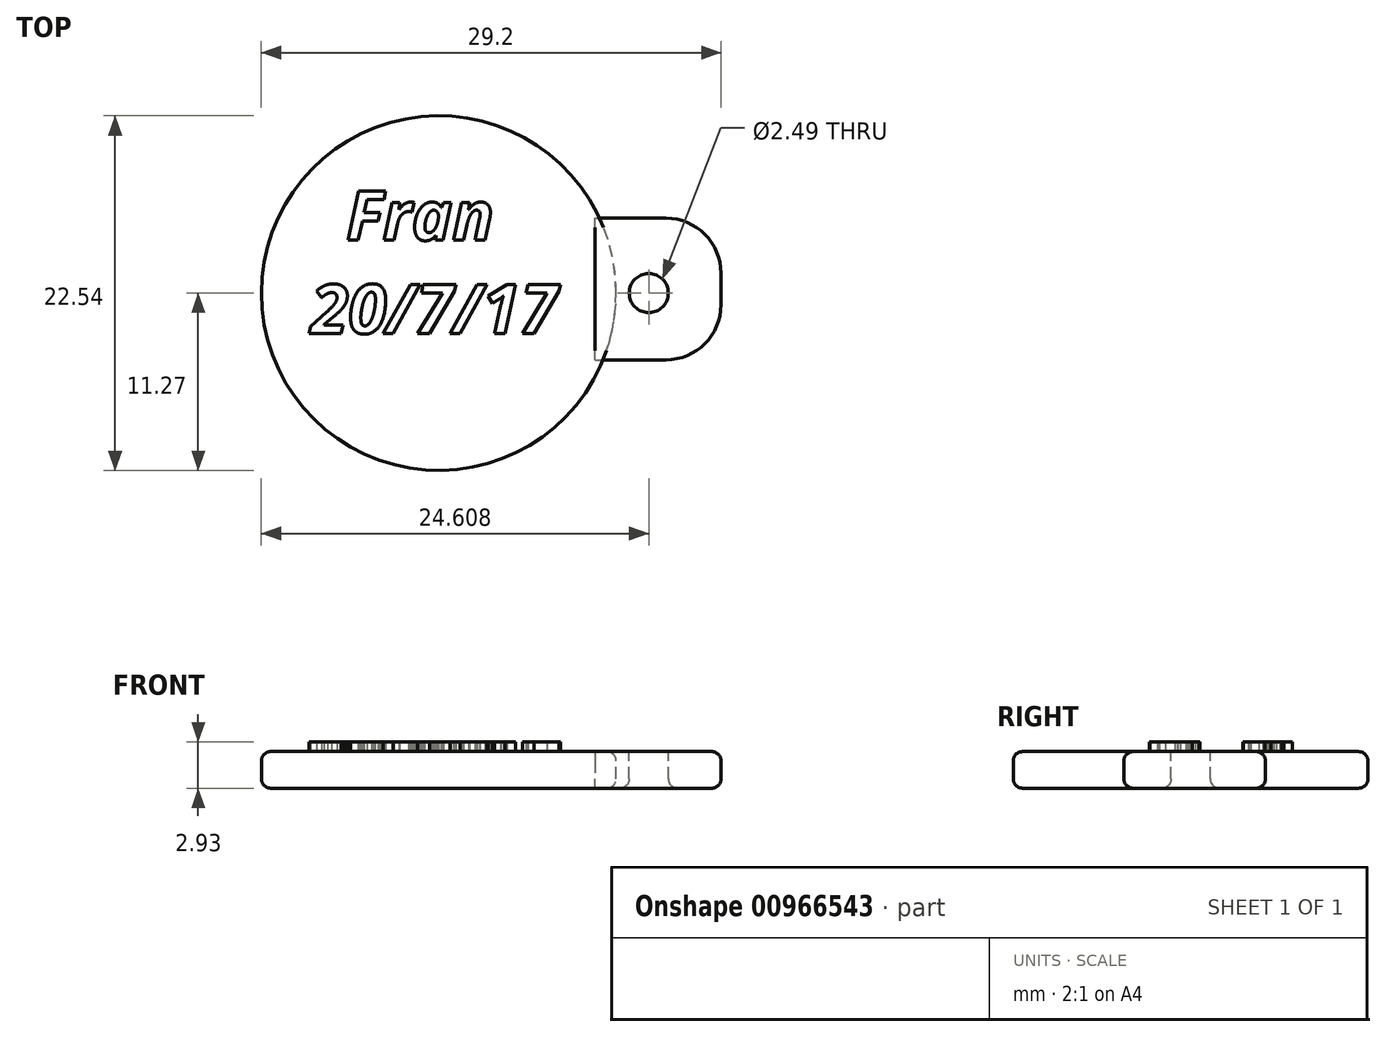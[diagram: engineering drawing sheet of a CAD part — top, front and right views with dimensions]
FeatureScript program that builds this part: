
annotation { "Feature Type Name" : "Feature", "Feature Type Description" : "" }
export const myFeature = defineFeature(function(context is Context, id is Id, definition is map)
    precondition{}
    {
        {
            var Q0;
            Q0=qCreatedBy(makeId("Front.planeOp"),FACE);
            var sketch = newSketch(context, id + "F0", { "sketchPlane" : qUnion([Q0])});
            skLineSegment(sketch, "E0", {"start": v(0, 0) * mm, "end": v(11.27, 0) * mm});
            skLineSegment(sketch, "E1", {"start": v(11.27, 0) * mm, "end": v(11.27, 2.33) * mm});
            skLineSegment(sketch, "E2", {"start": v(11.27, 2.33) * mm, "end": v(0, 2.33) * mm});
            skLineSegment(sketch, "E3", {"start": v(0, 2.33) * mm, "end": v(0, 0) * mm});
            skSolve(sketch);
        }
        {
            var Q0;
            Q0=makeQuery(id+"F0.imprint","IMPRINT",FACE,{"disambiguationData":[TD([[makeQuery(id+"F0.imprint","IMPRINT",EDGE,{"derivedFrom":sQuery(id+"F0.wireOp",EDGE,"E0")}),1.0]])]});
            var Q1;
            Q1=sQuery(id+"F0.wireOp",EDGE,"E3");
            revolve(context, id + "F1", {"surfaceOperationType" : NewSurfaceOperationType.NEW, "entities" : qUnion([Q0]), "axis" : qUnion([Q1]), "revolveType" : RevolveType.FULL});
        }
        {
            var Q0;
            Q0=makeQuery(id+"F1.opRevolve","SWEPT_FACE",FACE,{"disambiguationData":[OSD([sQuery(id+"F0.wireOp",EDGE,"E2")])]});
            var sketch = newSketch(context, id + "F2", { "sketchPlane" : qUnion([Q0])});
            skText(sketch, "E4", { "text": "  Fran\n20/7/17", "fontName": "OpenSans-BoldItalic.ttf"});
            const initialGuessF2  = {"E4": [-0.00814, 0.00336, 1, 0, 0.00314]};
            skSetInitialGuess(sketch, initialGuessF2);
            skSolve(sketch);
        }
        {
            var Q0;
            Q0 = qSketchRegion(id + "F2", true);
            extrude(context, id + "F3", {"entities" : qUnion([Q0]), "operationType" : NewBodyOperationType.ADD, "depth" : 0.6 * mm, "offsetDistance" : 25 * mm});
        }
        {
            var Q0;
            Q0=qCreatedBy(makeId("Top.planeOp"),FACE);
            var sketch = newSketch(context, id + "F4", { "sketchPlane" : qUnion([Q0])});
            skLineSegment(sketch, "E5.bottom", {"start": v(9.93, 4.76) * mm, "end": v(17.93, 4.76) * mm});
            skLineSegment(sketch, "E5.top", {"start": v(9.93, -4.24) * mm, "end": v(17.93, -4.24) * mm});
            skLineSegment(sketch, "E5.left", {"start": v(9.93, 4.76) * mm, "end": v(9.93, -4.24) * mm});
            skLineSegment(sketch, "E5.right", {"start": v(17.93, 4.76) * mm, "end": v(17.93, -4.24) * mm});
            skSolve(sketch);
        }
        {
            var Q0;
            Q0=makeQuery(id+"F4.imprint","IMPRINT",FACE,{"disambiguationData":[TD([[makeQuery(id+"F4.imprint","IMPRINT",EDGE,{"derivedFrom":sQuery(id+"F4.wireOp",EDGE,"E5.bottom")}),-1.0]])]});
            extrude(context, id + "F5", {"entities" : qUnion([Q0]), "depth" : 2.33 * mm, "offsetDistance" : 25 * mm});
        }
        {
            var Q0;
            Q0=makeQuery(id+"F5.opExtrude","CAP_FACE",FACE,{"disambiguationData":[OSD([sQuery(id+"F4.wireOp",EDGE,"E5.bottom"),sQuery(id+"F4.wireOp",EDGE,"E5.top"),sQuery(id+"F4.wireOp",EDGE,"E5.left"),sQuery(id+"F4.wireOp",EDGE,"E5.right")])],"isStart":false});
            var sketch = newSketch(context, id + "F6", { "sketchPlane" : qUnion([Q0])});
            skCircle(sketch, "E6", {"center": v(13.34, 0) * mm, "radius": 1.24 * mm});
            skSolve(sketch);
        }
        {
            var Q0;
            Q0=makeQuery(id+"F6.imprint","IMPRINT",FACE,{"disambiguationData":[TD([[makeQuery(id+"F6.imprint","IMPRINT",EDGE,{"derivedFrom":sQuery(id+"F6.wireOp",EDGE,"E6")}),1.0]])]});
            extrude(context, id + "F7", {"entities" : qUnion([Q0]), "operationType" : NewBodyOperationType.REMOVE, "endBound" : BoundingType.THROUGH_ALL, "oppositeDirection" : true, "depth" : 25 * mm, "offsetDistance" : 25 * mm});
        }
        {
            var Q0;
            Q0=makeQuery(id+"F5.opExtrude","SWEPT_EDGE",EDGE,{"disambiguationData":[OSD([sQuery(id+"F4.wireOp",EDGE,"E5.top"),sQuery(id+"F4.wireOp",EDGE,"E5.right")])]});
            var Q1;
            Q1=makeQuery(id+"F5.opExtrude","SWEPT_EDGE",EDGE,{"disambiguationData":[OSD([sQuery(id+"F4.wireOp",EDGE,"E5.bottom"),sQuery(id+"F4.wireOp",EDGE,"E5.right")])]});
            fillet(context, id + "F8", {"entities" : qUnion([Q0, Q1]), "radius" : 3.5 * mm, "tangentPropagation" : true, "allowEdgeOverflow" : false});
        }
        {
            var Q0;
            Q0=makeQuery(id+"F1.opRevolve","SWEPT_EDGE",EDGE,{"disambiguationData":[OSD([sQuery(id+"F0.wireOp",EDGE,"E1"),sQuery(id+"F0.wireOp",EDGE,"E2")])]});
            var Q1;
            Q1=makeQuery(id+"F5.opExtrude","CAP_EDGE",EDGE,{"disambiguationData":[OSD([sQuery(id+"F4.wireOp",EDGE,"E5.top")])],"isStart":false});
            var Q2;
            {var subQ0=sQuery(id+"F4.wireOp",EDGE,"E5.right");var subQ1=sQuery(id+"F4.wireOp",EDGE,"E5.top");Q2=makeQuery(id+"F8.opFillet","BLEND_EDGE",EDGE,{"blendedFrom":[makeQuery(id+"F5.opExtrude","SWEPT_EDGE",EDGE,{"disambiguationData":[OSD([subQ1,subQ0])]}),makeQuery(id+"F5.opExtrude","CAP_FACE",FACE,{"disambiguationData":[OSD([sQuery(id+"F4.wireOp",EDGE,"E5.bottom"),subQ1,sQuery(id+"F4.wireOp",EDGE,"E5.left"),subQ0])],"isStart":false})],"blendedInto":[makeQuery(id+"F5.opExtrude","CAP_FACE",FACE,{"disambiguationData":[OSD([sQuery(id+"F4.wireOp",EDGE,"E5.bottom"),subQ1,sQuery(id+"F4.wireOp",EDGE,"E5.left"),subQ0])],"isStart":false})]});}
            var Q3;
            Q3=makeQuery(id+"F5.opExtrude","CAP_EDGE",EDGE,{"disambiguationData":[OSD([sQuery(id+"F4.wireOp",EDGE,"E5.right")])],"isStart":false});
            var Q4;
            {var subQ0=sQuery(id+"F4.wireOp",EDGE,"E5.right");var subQ1=sQuery(id+"F4.wireOp",EDGE,"E5.bottom");Q4=makeQuery(id+"F8.opFillet","BLEND_EDGE",EDGE,{"blendedFrom":[makeQuery(id+"F5.opExtrude","SWEPT_EDGE",EDGE,{"disambiguationData":[OSD([subQ1,subQ0])]}),makeQuery(id+"F5.opExtrude","CAP_FACE",FACE,{"disambiguationData":[OSD([subQ1,sQuery(id+"F4.wireOp",EDGE,"E5.top"),sQuery(id+"F4.wireOp",EDGE,"E5.left"),subQ0])],"isStart":false})],"blendedInto":[makeQuery(id+"F5.opExtrude","CAP_FACE",FACE,{"disambiguationData":[OSD([subQ1,sQuery(id+"F4.wireOp",EDGE,"E5.top"),sQuery(id+"F4.wireOp",EDGE,"E5.left"),subQ0])],"isStart":false})]});}
            var Q5;
            Q5=makeQuery(id+"F5.opExtrude","CAP_EDGE",EDGE,{"disambiguationData":[OSD([sQuery(id+"F4.wireOp",EDGE,"E5.top")])],"isStart":true});
            var Q6;
            {var subQ0=sQuery(id+"F4.wireOp",EDGE,"E5.right");var subQ1=sQuery(id+"F4.wireOp",EDGE,"E5.top");Q6=makeQuery(id+"F8.opFillet","BLEND_EDGE",EDGE,{"blendedFrom":[makeQuery(id+"F5.opExtrude","SWEPT_EDGE",EDGE,{"disambiguationData":[OSD([subQ1,subQ0])]}),makeQuery(id+"F5.opExtrude","CAP_FACE",FACE,{"disambiguationData":[OSD([sQuery(id+"F4.wireOp",EDGE,"E5.bottom"),subQ1,sQuery(id+"F4.wireOp",EDGE,"E5.left"),subQ0])],"isStart":true})],"blendedInto":[makeQuery(id+"F5.opExtrude","CAP_FACE",FACE,{"disambiguationData":[OSD([sQuery(id+"F4.wireOp",EDGE,"E5.bottom"),subQ1,sQuery(id+"F4.wireOp",EDGE,"E5.left"),subQ0])],"isStart":true})]});}
            var Q7;
            Q7=makeQuery(id+"F5.opExtrude","CAP_EDGE",EDGE,{"disambiguationData":[OSD([sQuery(id+"F4.wireOp",EDGE,"E5.right")])],"isStart":true});
            var Q8;
            {var subQ0=sQuery(id+"F4.wireOp",EDGE,"E5.right");var subQ1=sQuery(id+"F4.wireOp",EDGE,"E5.bottom");Q8=makeQuery(id+"F8.opFillet","BLEND_EDGE",EDGE,{"blendedFrom":[makeQuery(id+"F5.opExtrude","SWEPT_EDGE",EDGE,{"disambiguationData":[OSD([subQ1,subQ0])]}),makeQuery(id+"F5.opExtrude","CAP_FACE",FACE,{"disambiguationData":[OSD([subQ1,sQuery(id+"F4.wireOp",EDGE,"E5.top"),sQuery(id+"F4.wireOp",EDGE,"E5.left"),subQ0])],"isStart":true})],"blendedInto":[makeQuery(id+"F5.opExtrude","CAP_FACE",FACE,{"disambiguationData":[OSD([subQ1,sQuery(id+"F4.wireOp",EDGE,"E5.top"),sQuery(id+"F4.wireOp",EDGE,"E5.left"),subQ0])],"isStart":true})]});}
            var Q9;
            Q9=makeQuery(id+"F1.opRevolve","SWEPT_EDGE",EDGE,{"disambiguationData":[OSD([sQuery(id+"F0.wireOp",EDGE,"E0"),sQuery(id+"F0.wireOp",EDGE,"E1")])]});
            var Q10;
            Q10=makeQuery(id+"F5.opExtrude","CAP_EDGE",EDGE,{"disambiguationData":[OSD([sQuery(id+"F4.wireOp",EDGE,"E5.bottom")])],"isStart":false});
            var Q11;
            Q11=makeQuery(id+"F7.boolean.opBoolean","COPY",EDGE,{"derivedFrom":makeQuery(id+"F7.opExtrude","CAP_EDGE",EDGE,{"disambiguationData":[OSD([sQuery(id+"F6.wireOp",EDGE,"E6")])],"isStart":true})});
            var Q12;
            Q12=makeQuery(id+"F5.opExtrude","CAP_EDGE",EDGE,{"disambiguationData":[OSD([sQuery(id+"F4.wireOp",EDGE,"E5.bottom")])],"isStart":true});
            var Q13;
            Q13=makeQuery(id+"F7.boolean.opBoolean","INTERSECT",EDGE,{"derivedFrom":[makeQuery(id+"F5.opExtrude","CAP_FACE",FACE,{"disambiguationData":[OSD([sQuery(id+"F4.wireOp",EDGE,"E5.bottom"),sQuery(id+"F4.wireOp",EDGE,"E5.top"),sQuery(id+"F4.wireOp",EDGE,"E5.left"),sQuery(id+"F4.wireOp",EDGE,"E5.right")])],"isStart":true}),makeQuery(id+"F7.opExtrude","SWEPT_FACE",FACE,{"disambiguationData":[OSD([sQuery(id+"F6.wireOp",EDGE,"E6")])]})]});
            var Q14;
            Q14=makeQuery(id+"FLPmNzv02p7TKbH_1.boolean.opBoolean","COPY",EDGE,{"derivedFrom":makeQuery(id+"FLPmNzv02p7TKbH_1.opExtrude","CAP_EDGE",EDGE,{"disambiguationData":[OSD([sQuery(id+"FIlv3tIL1fkSDHT_1.wireOp",EDGE,"TzbNWJEV-f2U4-Qj6M-bdTl-gwPe8NQgk8bM")])],"isStart":true})});
            var Q15;
            Q15=makeQuery(id+"FLPmNzv02p7TKbH_1.boolean.opBoolean","INTERSECT",EDGE,{"derivedFrom":[makeQuery(id+"F1.opRevolve","SWEPT_FACE",FACE,{"disambiguationData":[OSD([sQuery(id+"F0.wireOp",EDGE,"E0")])]}),makeQuery(id+"FLPmNzv02p7TKbH_1.opExtrude","SWEPT_FACE",FACE,{"disambiguationData":[OSD([sQuery(id+"FIlv3tIL1fkSDHT_1.wireOp",EDGE,"TzbNWJEV-f2U4-Qj6M-bdTl-gwPe8NQgk8bM")])]})]});
            fillet(context, id + "F9", {"entities" : qUnion([Q0, Q1, Q2, Q3, Q4, Q5, Q6, Q7, Q8, Q9, Q10, Q11, Q12, Q13, Q14, Q15]), "radius" : 0.6 * mm, "tangentPropagation" : true, "allowEdgeOverflow" : false});
        }
    });
